# Revit family: Keilhauer_Juxta_Benches_Stools_Star_Low_Back_Stool
name_source: partatom
category: Furniture
units: mm (PartAtom-declared; Revit-internal decimal feet)

## family parameters
Always vertical = Yes
Cut with Voids When Loaded = No
OmniClass Number = 23.40.70.14.64.11
OmniClass Title = Office Furniture
Room Calculation Point = No
Shared = No
Work Plane-Based = No

## types (2) — shared parameters
Assembly Code = E2020200
Catalog = JUXTA
Manufacturer = Keilhauer, Corp.
Product Documentation Link = http://www.keilhauer.com
URL = http://www.keilhauer.com
zero-valued in all types: Default Elevation

## per-type parameters (varying)
| type | B-Stool | C-Stool | Length 1 | Length 2 | Model |
| Counter Stool Backless with 4 Leg Base | No | Yes | 23.15 " | 23.53 " | 46712 |
| Bar Stool Backless with 4 Leg Base | Yes | No | 28.1 " | 28.48 " | 46713 |

note: column(s) folded — value = type name in every type: Description

## geometry (parser evidence)
native form markers: Sweep x4
no freeform markers — native parametric forms only
